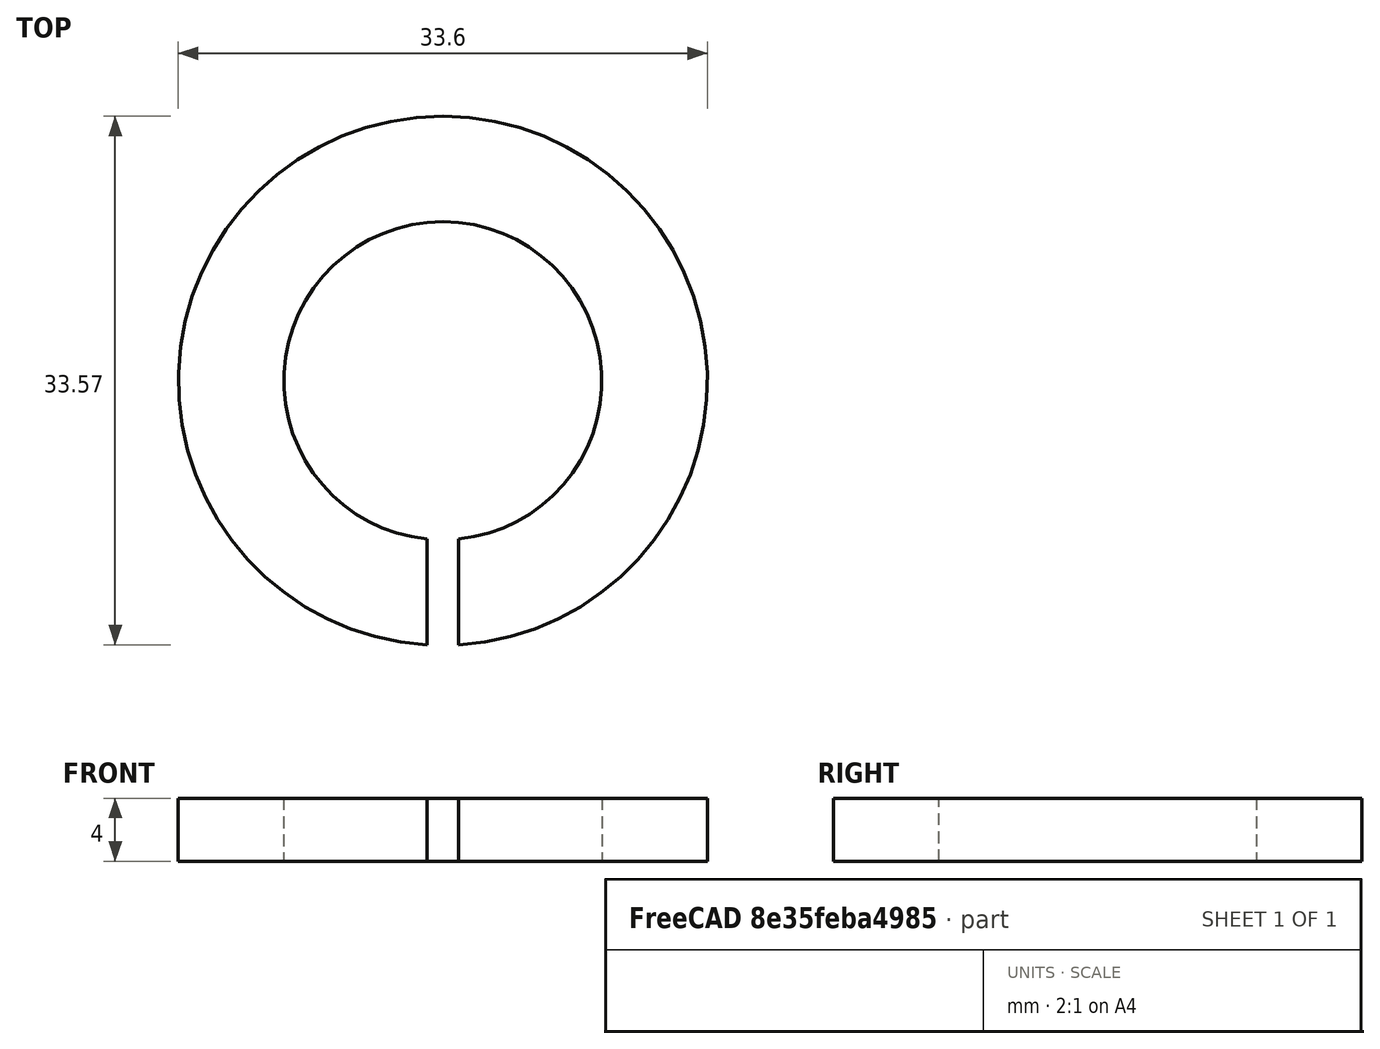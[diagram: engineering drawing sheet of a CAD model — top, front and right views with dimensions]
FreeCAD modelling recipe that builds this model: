
FCSTD DOCUMENT  (FreeCAD 0.15R4651 (Git))
Label: Federring_DIN127-B20
License: All rights reserved
LicenseURL: http://de.wikipedia.org/wiki/Alle_Rechte_vorbehalten
objects: Sketcher::SketchObject×1, PartDesign::Pad×1
note: 3 computed .brp shape members not serialized (recipe doc carries the construction recipe); baked Part::Feature solids carry a one-line shape summary decoded from their .brp

FEATURE [Sketcher::SketchObject] Sketch
  sketch-geometry (4):
    g0: ArcOfCircle CenterX=0 CenterY=0 CenterZ=0 NormalX=0 NormalY=0 NormalZ=1 Radius=10.1 StartAngle=4.81156 EndAngle=10.8964
    g1: ArcOfCircle CenterX=0 CenterY=0 CenterZ=0 NormalX=0 NormalY=0 NormalZ=1 Radius=16.8 StartAngle=4.77195 EndAngle=10.936
    g2: LineSegment StartX=1 StartY=-10.0504 StartZ=0 EndX=1 EndY=-16.7702 EndZ=0
    g3: LineSegment StartX=-1 StartY=-16.7702 StartZ=0 EndX=-1 EndY=-10.0504 EndZ=0
  constraints (12):
    c: Coincident(g0,g-1)
    c: Coincident(g1,g-1)
    c: Vertical(g2)
    c: Vertical(g3)
    c: Coincident(g0,g2)
    c: Coincident(g0,g3)
    c: Coincident(g1,g2)
    c: Coincident(g1,g3)
    c: Symmetric(g1,g1,g-2)
    c: Radius(g0) = 10.1
    c: Radius(g1) = 16.8
    c: DistanceX(g1,g1) = -2
FEATURE [PartDesign::Pad] Pad  label="Federring DIN 127-B 20 #"
  Length = 4
  Length2 = 100
  Midplane = true
  Sketch = -> Sketch
  Type = 0
